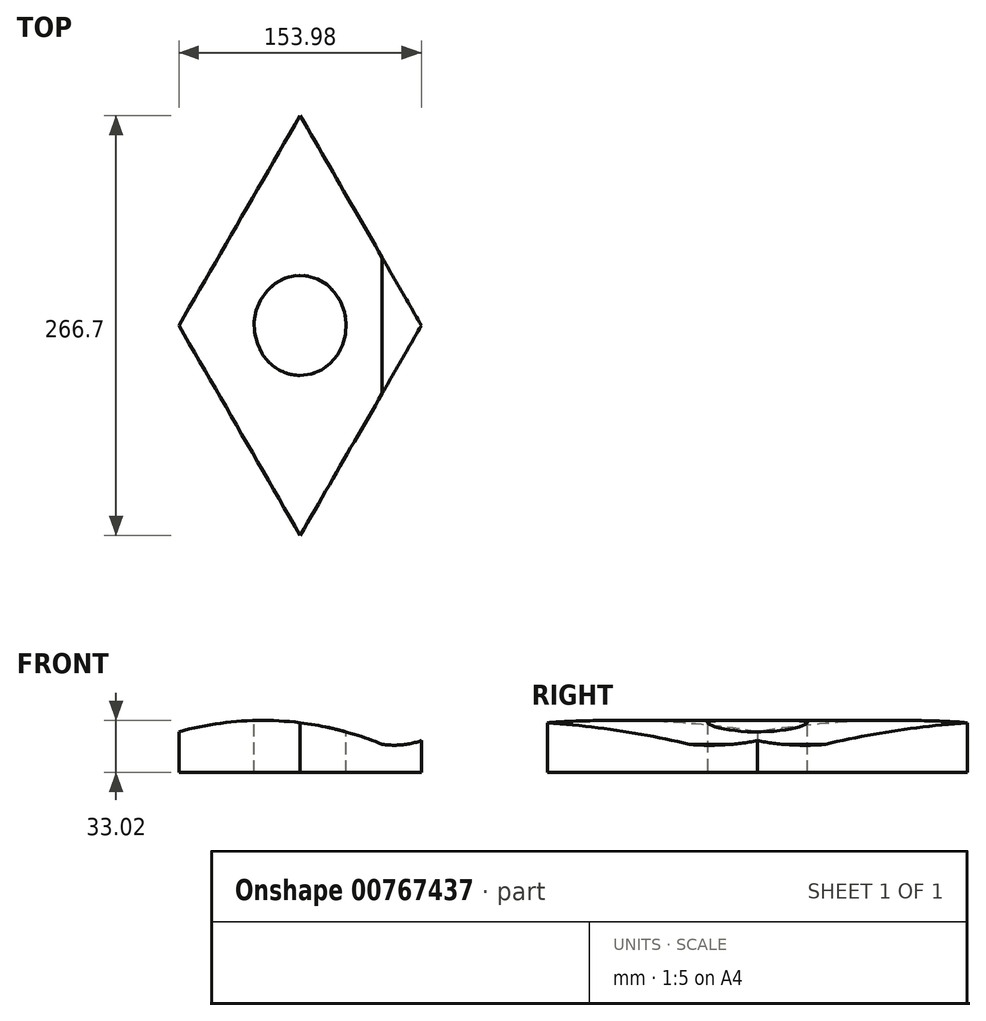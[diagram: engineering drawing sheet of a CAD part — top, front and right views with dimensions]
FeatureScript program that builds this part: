
annotation { "Feature Type Name" : "Feature", "Feature Type Description" : "" }
export const myFeature = defineFeature(function(context is Context, id is Id, definition is map)
    precondition{}
    {
        {
            var Q0;
            Q0=qCreatedBy(makeId("Front.planeOp"),FACE);
            var sketch = newSketch(context, id + "F0", { "sketchPlane" : qUnion([Q0])});
            skArc(sketch, "E0", {"start": v(22.86, 17.78) * mm, "mid": v(-53.34, 33.02) * mm, "end": v(-129.54, 17.78) * mm});
            skArc(sketch, "E1", {"start": v(22.86, 17.78) * mm, "mid": v(35.71, 17.52) * mm, "end": v(48.26, 20.32) * mm});
            skLineSegment(sketch, "E2", {"start": v(-129.54, 17.78) * mm, "end": v(-129.54, 0) * mm});
            skLineSegment(sketch, "E3", {"start": v(-129.54, 0) * mm, "end": v(48.26, 0) * mm});
            skLineSegment(sketch, "E4", {"start": v(48.26, 0) * mm, "end": v(48.26, 20.32) * mm});
            skLineSegment(sketch, "E5", {"start": v(0, 25.7) * mm, "end": v(0, 0) * mm});
            skSolve(sketch);
        }
        {
            var Q0;
            Q0=makeQuery(id+"F0.imprint","IMPRINT",FACE,{"disambiguationData":[TD([[makeQuery(id+"F0.imprint","IMPRINT",EDGE,{"derivedFrom":sQuery(id+"F0.wireOp",EDGE,"E0")}),1.0]])]});
            var Q1;
            {var subQ1=sQuery(id+"F0.wireOp",EDGE,"E1");Q1=makeQuery(id+"F0.imprint","IMPRINT",FACE,{"disambiguationData":[TD([[makeQuery(id+"F0.imprint","IMPRINT",EDGE,{"derivedFrom":subQ1}),-1.0]])]});}
            extrude(context, id + "F1", {"entities" : qUnion([Q0, Q1]), "depth" : 266.7 * mm, "offsetDistance" : 25.4 * mm});
        }
        {
            var Q0;
            Q0=makeQuery(id+"F0.imprint","IMPRINT",FACE,{"disambiguationData":[TD([[makeQuery(id+"F0.imprint","IMPRINT",EDGE,{"derivedFrom":sQuery(id+"F0.wireOp",EDGE,"E0")}),1.0]])]});
            extrude(context, id + "F2", {"entities" : qUnion([Q0]), "operationType" : NewBodyOperationType.ADD, "depth" : 266.7 * mm, "offsetDistance" : 25.4 * mm});
        }
        {
            var Q0;
            Q0=qCreatedBy(makeId("Top.planeOp"),FACE);
            var sketch = newSketch(context, id + "F3", { "sketchPlane" : qUnion([Q0])});
            skLineSegment(sketch, "E6", {"start": v(-29.2, 0) * mm, "end": v(47.78, -133.35) * mm});
            skLineSegment(sketch, "E7", {"start": v(-29.2, 0) * mm, "end": v(-106.2, -133.35) * mm});
            skLineSegment(sketch, "E8", {"start": v(-106.2, -133.35) * mm, "end": v(-29.2, -266.7) * mm});
            skLineSegment(sketch, "E9", {"start": v(47.78, -133.35) * mm, "end": v(-29.2, -266.7) * mm});
            skEllipse(sketch, "E10", {"center": v(-29.2, -133.35) * mm, "majorRadius": 31.75 * mm, "minorRadius": 29.21 * mm, "majorAxis": v(0, -1)});
            skSolve(sketch);
        }
        {
            var Q0;
            Q0=makeQuery(id+"F3.imprint","IMPRINT",FACE,{"disambiguationData":[TD([[makeQuery(id+"F3.imprint","IMPRINT",EDGE,{"derivedFrom":sQuery(id+"F3.wireOp",EDGE,"E6")}),-1.0]])]});
            extrude(context, id + "F4", {"entities" : qUnion([Q0]), "depth" : 33.02 * mm, "offsetDistance" : 25.4 * mm});
        }
        {
            var Q0;
            Q0=makeQuery(id+"F4.opExtrude","SWEPT_BODY",BODY,{"disambiguationData":[OSD([sQuery(id+"F3.wireOp",EDGE,"E6"),sQuery(id+"F3.wireOp",EDGE,"E7"),sQuery(id+"F3.wireOp",EDGE,"E8"),sQuery(id+"F3.wireOp",EDGE,"E9"),sQuery(id+"F3.wireOp",EDGE,"E10")])]});
            var Q1;
            Q1=makeQuery(id+"F1.opExtrude","SWEPT_BODY",BODY,{"disambiguationData":[OSD([sQuery(id+"F0.wireOp",EDGE,"E0"),sQuery(id+"F0.wireOp",EDGE,"E1"),sQuery(id+"F0.wireOp",EDGE,"E2"),sQuery(id+"F0.wireOp",EDGE,"E3"),sQuery(id+"F0.wireOp",EDGE,"E4")])]});
            booleanBodies(context, id + "F5", {"operationType" : BooleanOperationType.INTERSECTION, "tools" : qUnion([Q0, Q1])});
        }
    });
